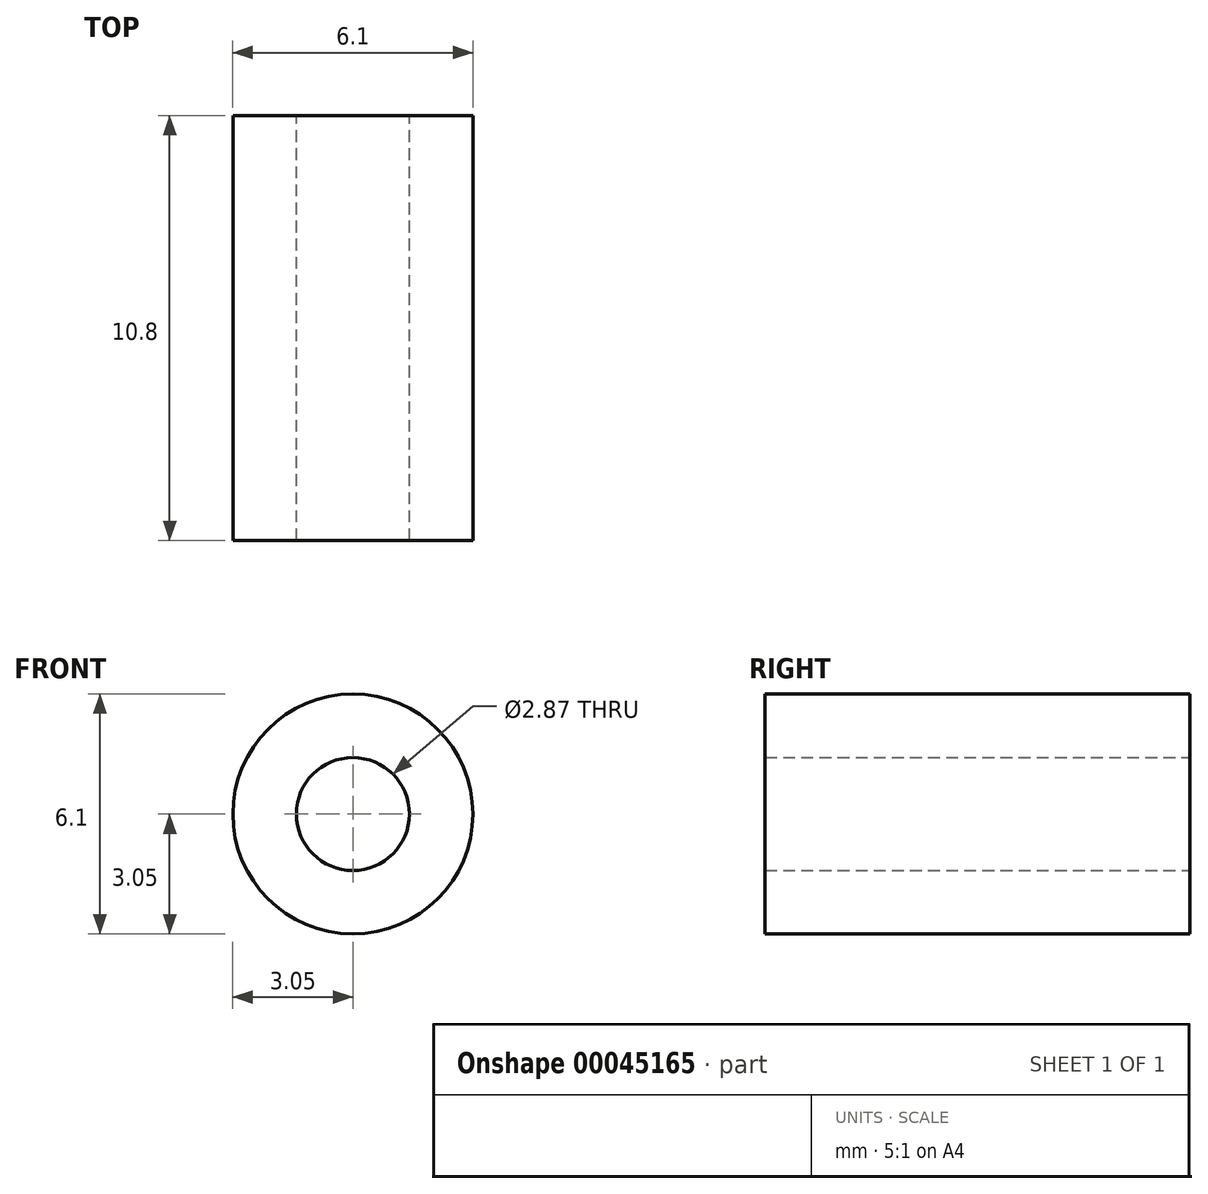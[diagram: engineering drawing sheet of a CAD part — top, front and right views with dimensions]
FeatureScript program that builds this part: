
annotation { "Feature Type Name" : "Feature", "Feature Type Description" : "" }
export const myFeature = defineFeature(function(context is Context, id is Id, definition is map)
    precondition{}
    {
        {
            var Q0;
            Q0=qCreatedBy(makeId("Front.planeOp"),FACE);
            var sketch = newSketch(context, id + "F0", { "sketchPlane" : qUnion([Q0])});
            skLineSegment(sketch, "E0", {"start": v(0, 0) * mm, "end": v(1.44, 0) * mm, "construction": true});
            skLineSegment(sketch, "E1", {"start": v(0, 0) * mm, "end": v(3.05, 0) * mm, "construction": true});
            skCircle(sketch, "E2", {"center": v(0, 0) * mm, "radius": 3.05 * mm});
            skPoint(sketch, "E3.0.midPoint", {"position": v(1.44, 0) * mm});
            skCircle(sketch, "E4", {"center": v(0, 0) * mm, "radius": 1.44 * mm});
            skLineSegment(sketch, "E5", {"start": v(-1.8, 2.45) * mm, "end": v(1.8, 2.45) * mm, "construction": true});
            skLineSegment(sketch, "E6", {"start": v(1.8, 2.45) * mm, "end": v(1.8, -2.45) * mm, "construction": true});
            skLineSegment(sketch, "E7", {"start": v(1.8, -2.45) * mm, "end": v(-1.8, -2.45) * mm, "construction": true});
            skLineSegment(sketch, "E8", {"start": v(-1.8, -2.45) * mm, "end": v(-1.8, 2.45) * mm, "construction": true});
            skLineSegment(sketch, "E9", {"start": v(-3.05, 0) * mm, "end": v(3.05, 0) * mm, "construction": true});
            skLineSegment(sketch, "E10", {"start": v(0, 3.05) * mm, "end": v(0, -3.05) * mm, "construction": true});
            skSolve(sketch);
        }
        {
            var Q0;
            Q0=qSketchRegion(id+"F0",true);
            extrude(context, id + "F1", {"entities" : qUnion([Q0]), "depth" : 10.8 * mm});
        }
    });
